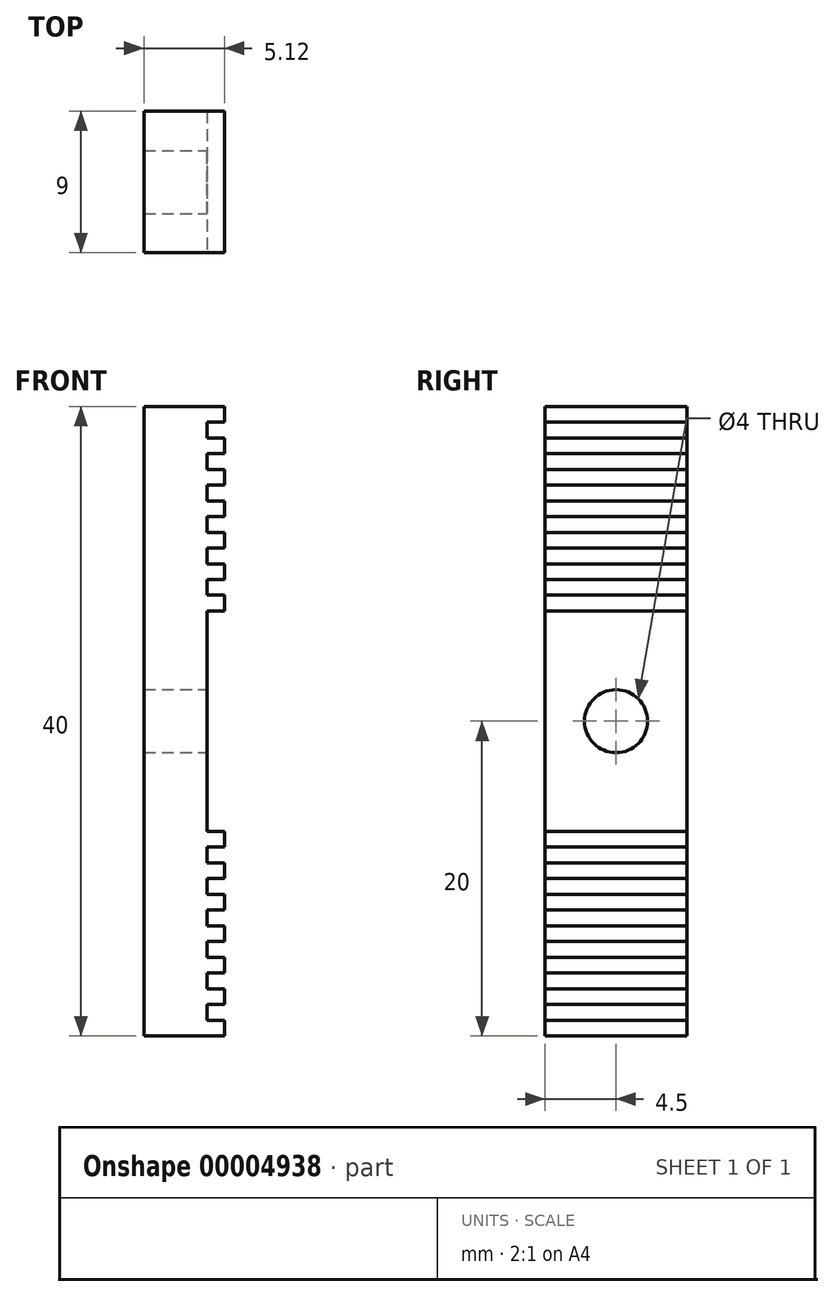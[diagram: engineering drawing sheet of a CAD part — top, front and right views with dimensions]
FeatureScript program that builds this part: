
annotation { "Feature Type Name" : "Feature", "Feature Type Description" : "" }
export const myFeature = defineFeature(function(context is Context, id is Id, definition is map)
    precondition{}
    {
        {
            var Q0;
            Q0=qCreatedBy(makeId("Front.planeOp"),FACE);
            var sketch = newSketch(context, id + "F0", { "sketchPlane" : qUnion([Q0])});
            skLineSegment(sketch, "E0.bottom", {"start": v(2, 20) * mm, "end": v(-2, 20) * mm});
            skLineSegment(sketch, "E0.top", {"start": v(2, -20) * mm, "end": v(-2, -20) * mm});
            skLineSegment(sketch, "E0.left", {"start": v(2, 20) * mm, "end": v(2, -20) * mm});
            skLineSegment(sketch, "E0.right", {"start": v(-2, 20) * mm, "end": v(-2, -20) * mm});
            skPoint(sketch, "E0.middle", {"position": v(0, 0) * mm});
            skSolve(sketch);
        }
        {
            var Q0;
            Q0 = qSketchRegion(id + "F0", true);
            extrude(context, id + "F1", {"entities" : qUnion([Q0]), "depth" : 9 * mm, "offsetDistance" : 25 * mm, "symmetric" : true});
        }
        {
            var Q0;
            Q0=makeQuery(id+"F1.opExtrude","CAP_FACE",FACE,{"disambiguationData":[OSD([sQuery(id+"F0.wireOp",EDGE,"E0.bottom"),sQuery(id+"F0.wireOp",EDGE,"E0.top"),sQuery(id+"F0.wireOp",EDGE,"E0.left"),sQuery(id+"F0.wireOp",EDGE,"E0.right")])],"isStart":false});
            var sketch = newSketch(context, id + "F2", { "sketchPlane" : qUnion([Q0])});
            skLineSegment(sketch, "E1", {"start": v(-2, 0) * mm, "end": v(2, 0) * mm, "construction": true});
            skLineSegment(sketch, "E2.bottom", {"start": v(2, 20) * mm, "end": v(3.13, 20) * mm});
            skLineSegment(sketch, "E2.top", {"start": v(2, 19) * mm, "end": v(3.13, 19) * mm});
            skLineSegment(sketch, "E2.left", {"start": v(2, 20) * mm, "end": v(2, 19) * mm});
            skLineSegment(sketch, "E2.right", {"start": v(3.13, 20) * mm, "end": v(3.13, 19) * mm});
            skLineSegment(sketch, "E3.1.0.0", {"start": v(3.13, 18) * mm, "end": v(3.13, 17) * mm});
            skLineSegment(sketch, "E3.1.0.1", {"start": v(2, 18) * mm, "end": v(3.13, 18) * mm});
            skLineSegment(sketch, "E3.1.0.2", {"start": v(2, 17) * mm, "end": v(3.13, 17) * mm});
            skLineSegment(sketch, "E3.1.0.3", {"start": v(2, 18) * mm, "end": v(2, 17) * mm});
            skLineSegment(sketch, "E3.2.0.0", {"start": v(3.13, 16) * mm, "end": v(3.13, 15) * mm});
            skLineSegment(sketch, "E3.2.0.1", {"start": v(2, 16) * mm, "end": v(3.13, 16) * mm});
            skLineSegment(sketch, "E3.2.0.2", {"start": v(2, 15) * mm, "end": v(3.13, 15) * mm});
            skLineSegment(sketch, "E3.2.0.3", {"start": v(2, 16) * mm, "end": v(2, 15) * mm});
            skLineSegment(sketch, "E3.3.0.0", {"start": v(3.13, 14) * mm, "end": v(3.13, 13) * mm});
            skLineSegment(sketch, "E3.3.0.1", {"start": v(2, 14) * mm, "end": v(3.13, 14) * mm});
            skLineSegment(sketch, "E3.3.0.2", {"start": v(2, 13) * mm, "end": v(3.13, 13) * mm});
            skLineSegment(sketch, "E3.3.0.3", {"start": v(2, 14) * mm, "end": v(2, 13) * mm});
            skLineSegment(sketch, "E3.4.0.0", {"start": v(3.13, 12) * mm, "end": v(3.13, 11) * mm});
            skLineSegment(sketch, "E3.4.0.1", {"start": v(2, 12) * mm, "end": v(3.13, 12) * mm});
            skLineSegment(sketch, "E3.4.0.2", {"start": v(2, 11) * mm, "end": v(3.13, 11) * mm});
            skLineSegment(sketch, "E3.4.0.3", {"start": v(2, 12) * mm, "end": v(2, 11) * mm});
            skLineSegment(sketch, "E3.5.0.0", {"start": v(3.13, 10) * mm, "end": v(3.13, 9) * mm});
            skLineSegment(sketch, "E3.5.0.1", {"start": v(2, 10) * mm, "end": v(3.13, 10) * mm});
            skLineSegment(sketch, "E3.5.0.2", {"start": v(2, 9) * mm, "end": v(3.13, 9) * mm});
            skLineSegment(sketch, "E3.5.0.3", {"start": v(2, 10) * mm, "end": v(2, 9) * mm});
            skLineSegment(sketch, "E3.6.0.0", {"start": v(3.13, 8) * mm, "end": v(3.13, 7) * mm});
            skLineSegment(sketch, "E3.6.0.1", {"start": v(2, 8) * mm, "end": v(3.13, 8) * mm});
            skLineSegment(sketch, "E3.6.0.2", {"start": v(2, 7) * mm, "end": v(3.13, 7) * mm});
            skLineSegment(sketch, "E3.6.0.3", {"start": v(2, 8) * mm, "end": v(2, 7) * mm});
            skLineSegment(sketch, "E3.direction1", {"start": v(2, 19) * mm, "end": v(2, 17) * mm, "construction": true});
            skLineSegment(sketch, "E4.MirrorCS", {"start": v(2, -19) * mm, "end": v(2, -17) * mm, "construction": true});
            skLineSegment(sketch, "E5.MirrorCS", {"start": v(2, -20) * mm, "end": v(2, -19) * mm});
            skLineSegment(sketch, "E6.MirrorCS", {"start": v(2, -8) * mm, "end": v(2, -7) * mm});
            skLineSegment(sketch, "E7.MirrorCS", {"start": v(3.13, -16) * mm, "end": v(3.13, -15) * mm});
            skLineSegment(sketch, "E8.MirrorCS", {"start": v(3.13, -8) * mm, "end": v(3.13, -7) * mm});
            skLineSegment(sketch, "E9.MirrorCS", {"start": v(2, -16) * mm, "end": v(3.13, -16) * mm});
            skLineSegment(sketch, "E10.MirrorCS", {"start": v(2, -13) * mm, "end": v(3.13, -13) * mm});
            skLineSegment(sketch, "E11.MirrorCS", {"start": v(2, -12) * mm, "end": v(3.13, -12) * mm});
            skLineSegment(sketch, "E12.MirrorCS", {"start": v(2, -10) * mm, "end": v(2, -9) * mm});
            skLineSegment(sketch, "E13.MirrorCS", {"start": v(3.13, -14) * mm, "end": v(3.13, -13) * mm});
            skLineSegment(sketch, "E14.MirrorCS", {"start": v(3.13, -12) * mm, "end": v(3.13, -11) * mm});
            skLineSegment(sketch, "E15.MirrorCS", {"start": v(2, -15) * mm, "end": v(3.13, -15) * mm});
            skLineSegment(sketch, "E16.MirrorCS", {"start": v(2, -9) * mm, "end": v(3.13, -9) * mm});
            skLineSegment(sketch, "E17.MirrorCS", {"start": v(2, -12) * mm, "end": v(2, -11) * mm});
            skLineSegment(sketch, "E18.MirrorCS", {"start": v(2, -14) * mm, "end": v(3.13, -14) * mm});
            skLineSegment(sketch, "E19.MirrorCS", {"start": v(2, -16) * mm, "end": v(2, -15) * mm});
            skLineSegment(sketch, "E20.MirrorCS", {"start": v(2, -18) * mm, "end": v(2, -17) * mm});
            skLineSegment(sketch, "E21.MirrorCS", {"start": v(2, -19) * mm, "end": v(3.13, -19) * mm});
            skLineSegment(sketch, "E22.MirrorCS", {"start": v(2, -17) * mm, "end": v(3.13, -17) * mm});
            skLineSegment(sketch, "E23.MirrorCS", {"start": v(2, -14) * mm, "end": v(2, -13) * mm});
            skLineSegment(sketch, "E24.MirrorCS", {"start": v(2, -18) * mm, "end": v(3.13, -18) * mm});
            skLineSegment(sketch, "E25.MirrorCS", {"start": v(3.13, -18) * mm, "end": v(3.13, -17) * mm});
            skLineSegment(sketch, "E26.MirrorCS", {"start": v(2, -10) * mm, "end": v(3.13, -10) * mm});
            skLineSegment(sketch, "E27.MirrorCS", {"start": v(2, -8) * mm, "end": v(3.13, -8) * mm});
            skLineSegment(sketch, "E28.MirrorCS", {"start": v(2, -20) * mm, "end": v(3.13, -20) * mm});
            skLineSegment(sketch, "E29.MirrorCS", {"start": v(2, -11) * mm, "end": v(3.13, -11) * mm});
            skLineSegment(sketch, "E30.MirrorCS", {"start": v(3.13, -20) * mm, "end": v(3.13, -19) * mm});
            skLineSegment(sketch, "E31.MirrorCS", {"start": v(2, -7) * mm, "end": v(3.13, -7) * mm});
            skLineSegment(sketch, "E32.MirrorCS", {"start": v(3.13, -10) * mm, "end": v(3.13, -9) * mm});
            skSolve(sketch);
        }
        {
            var Q0;
            Q0 = qSketchRegion(id + "F2", true);
            var Q1;
            Q1=makeQuery(id+"F1.opExtrude","CAP_FACE",FACE,{"disambiguationData":[OSD([sQuery(id+"F0.wireOp",EDGE,"E0.bottom"),sQuery(id+"F0.wireOp",EDGE,"E0.top"),sQuery(id+"F0.wireOp",EDGE,"E0.left"),sQuery(id+"F0.wireOp",EDGE,"E0.right")])],"isStart":true});
            extrude(context, id + "F3", {"entities" : qUnion([Q0]), "operationType" : NewBodyOperationType.ADD, "endBound" : BoundingType.UP_TO_SURFACE, "oppositeDirection" : true, "depth" : 25 * mm, "endBoundEntityFace" : qUnion([Q1]), "offsetDistance" : 25 * mm});
        }
        {
            var Q0;
            {var subQ4=sQuery(id+"F2.wireOp",EDGE,"E3.6.0.2");var subQ37=sQuery(id+"F0.wireOp",EDGE,"E0.left");Q0=makeQuery(id+"F3.boolean.opBoolean","SPLIT",FACE,{"disambiguationData":[TD([makeQuery(id+"F3.opExtrude","SWEPT_FACE",FACE,{"disambiguationData":[OSD([subQ4])]})])],"derivedFrom":makeQuery(id+"F1.opExtrude","SWEPT_FACE",FACE,{"disambiguationData":[OSD([subQ37])]})});}
            var sketch = newSketch(context, id + "F4", { "sketchPlane" : qUnion([Q0])});
            skCircle(sketch, "E33", {"center": v(0, 0) * mm, "radius": 2 * mm});
            skSolve(sketch);
        }
        {
            var Q0;
            Q0 = qSketchRegion(id + "F4", true);
            extrude(context, id + "F5", {"entities" : qUnion([Q0]), "operationType" : NewBodyOperationType.REMOVE, "endBound" : BoundingType.THROUGH_ALL, "oppositeDirection" : true, "depth" : 25 * mm, "offsetDistance" : 25 * mm});
        }
    });
